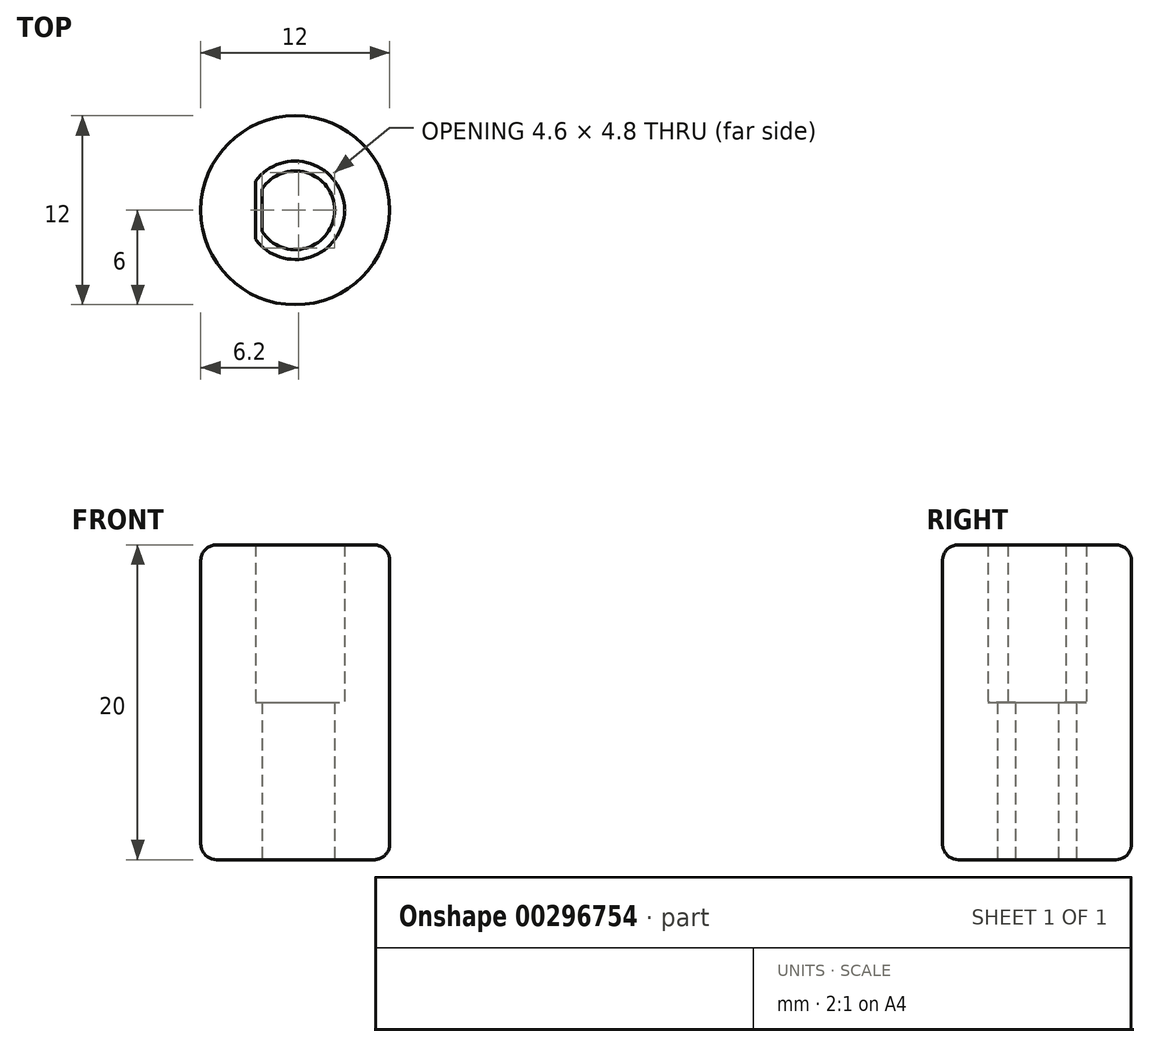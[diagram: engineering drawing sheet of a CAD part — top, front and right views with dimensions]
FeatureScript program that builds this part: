
annotation { "Feature Type Name" : "Feature", "Feature Type Description" : "" }
export const myFeature = defineFeature(function(context is Context, id is Id, definition is map)
    precondition{}
    {
        {
            var Q0;
            Q0=qCreatedBy(makeId("Top.planeOp"),FACE);
            var sketch = newSketch(context, id + "F0", { "sketchPlane" : qUnion([Q0])});
            skArc(sketch, "E0", {"start": v(-2.53, -1.84) * mm, "mid": v(3.12, 0) * mm, "end": v(-2.52, 1.84) * mm});
            skLineSegment(sketch, "E1", {"start": v(-2.53, -1.84) * mm, "end": v(-2.53, 1.84) * mm});
            skCircle(sketch, "E2", {"center": v(0, 0) * mm, "radius": 6 * mm});
            skSolve(sketch);
        }
        {
            var Q0;
            Q0=makeQuery(id+"F0.imprint","IMPRINT",FACE,{"disambiguationData":[TD([[makeQuery(id+"F0.imprint","IMPRINT",EDGE,{"derivedFrom":sQuery(id+"F0.wireOp",EDGE,"E0")}),-1.0]])]});
            extrude(context, id + "F1", {"entities" : qUnion([Q0]), "depth" : 20 * mm});
        }
        {
            var Q0;
            Q0=makeQuery(id+"F0.imprint","IMPRINT",FACE,{"disambiguationData":[TD([[makeQuery(id+"F0.imprint","IMPRINT",EDGE,{"derivedFrom":sQuery(id+"F0.wireOp",EDGE,"E0")}),1.0]])]});
            extrude(context, id + "F2", {"entities" : qUnion([Q0]), "operationType" : NewBodyOperationType.ADD, "depth" : 10 * mm});
        }
        {
            var Q0;
            {var subQ0=sQuery(id+"F0.wireOp",EDGE,"E1");var subQ1=sQuery(id+"F0.wireOp",EDGE,"E0");Q0=makeQuery(id+"F2.boolean.opBoolean","MERGE",FACE,{"derivedFrom":[makeQuery(id+"F1.opExtrude","CAP_FACE",FACE,{"disambiguationData":[OSD([subQ1,subQ0,sQuery(id+"F0.wireOp",EDGE,"E2")])],"isStart":true}),makeQuery(id+"F2.opExtrude","CAP_FACE",FACE,{"disambiguationData":[OSD([subQ1,subQ0])],"isStart":true})]});}
            var sketch = newSketch(context, id + "F3", { "sketchPlane" : qUnion([Q0])});
            skArc(sketch, "E3", {"start": v(-2.1, -1.36) * mm, "mid": v(2.5, 0) * mm, "end": v(-2.1, 1.36) * mm});
            skLineSegment(sketch, "E4", {"start": v(-2.1, -1.36) * mm, "end": v(-2.1, 1.36) * mm});
            skSolve(sketch);
        }
        {
            var Q0;
            Q0=makeQuery(id+"F3.imprint","IMPRINT",FACE,{"disambiguationData":[TD([[makeQuery(id+"F3.imprint","IMPRINT",EDGE,{"derivedFrom":sQuery(id+"F3.wireOp",EDGE,"E3")}),1.0]])]});
            extrude(context, id + "F4", {"entities" : qUnion([Q0]), "operationType" : NewBodyOperationType.REMOVE, "oppositeDirection" : true, "depth" : 25 * mm});
        }
        {
            var Q0;
            Q0=makeQuery(id+"F1.opExtrude","CAP_EDGE",EDGE,{"disambiguationData":[OSD([sQuery(id+"F0.wireOp",EDGE,"E2")])],"isStart":false});
            var Q1;
            Q1=makeQuery(id+"F1.opExtrude","CAP_EDGE",EDGE,{"disambiguationData":[OSD([sQuery(id+"F0.wireOp",EDGE,"E2")])],"isStart":true});
            fillet(context, id + "F5", {"entities" : qUnion([Q0, Q1]), "radius" : 1 * mm, "tangentPropagation" : true, "allowEdgeOverflow" : false});
        }
    });
